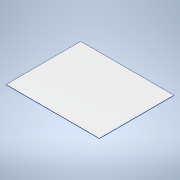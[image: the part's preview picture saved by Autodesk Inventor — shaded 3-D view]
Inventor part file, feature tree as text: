
AUTODESK INVENTOR PART (.ipt)
format: ipt  version: 2020 (Build 240168000, 168)  size: 93,184 bytes
history: native  units: mm
features: other x1, extrude x1, sketch x1
ambient origin geometry x8: Origin, YZ Plane, XZ Plane, XY Plane, X Axis, Y Axis, Z Axis, Center Point
bodies: Body1 (feature_tree)
feature tree (3):
  other  "Bryła1"
  extrude  "Wyciągnięcie proste1"  Depth=800.0mm
  sketch  "Szkic1"
